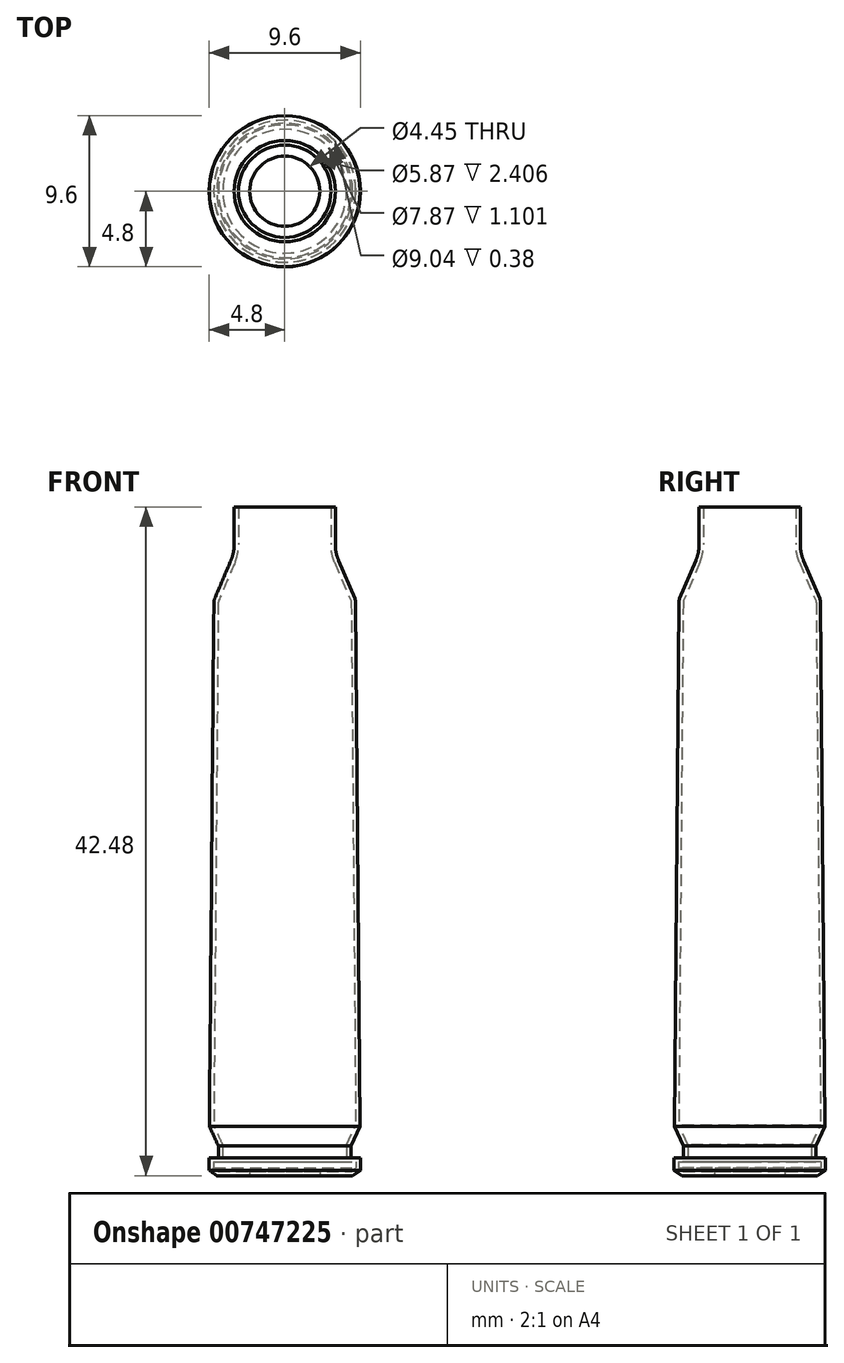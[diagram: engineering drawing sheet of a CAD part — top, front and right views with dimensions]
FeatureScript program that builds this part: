
annotation { "Feature Type Name" : "Feature", "Feature Type Description" : "" }
export const myFeature = defineFeature(function(context is Context, id is Id, definition is map)
    precondition{}
    {
        {
            var Q0;
            Q0=qCreatedBy(makeId("Front.planeOp"),FACE);
            var sketch = newSketch(context, id + "F0", { "sketchPlane" : qUnion([Q0])});
            skLineSegment(sketch, "E0", {"start": v(4.31, -41.16) * mm, "end": v(4.8, -40.82) * mm});
            skLineSegment(sketch, "E1", {"start": v(4.8, -40.82) * mm, "end": v(4.8, -40.01) * mm});
            skLineSegment(sketch, "E2", {"start": v(4.8, -40.01) * mm, "end": v(4.22, -40.01) * mm});
            skLineSegment(sketch, "E3", {"start": v(4.22, -40.01) * mm, "end": v(4.22, -39.25) * mm});
            skLineSegment(sketch, "E4", {"start": v(4.22, -39.25) * mm, "end": v(4.79, -38.02) * mm});
            skLineSegment(sketch, "E5", {"start": v(4.79, -38.02) * mm, "end": v(4.5, -4.76) * mm});
            skPoint(sketch, "E6", {"position": v(0, 5.97) * mm});
            skLineSegment(sketch, "E7", {"start": v(4.45, -4.52) * mm, "end": v(3.42, -2.08) * mm});
            skLineSegment(sketch, "E8", {"start": v(3.22, 1.32) * mm, "end": v(3.22, -1.09) * mm});
            skPoint(sketch, "E9.visualSharp", {"position": v(4.5, -4.63) * mm});
            skArc(sketch, "E9.filletArc", {"start": v(4.5, -4.76) * mm, "mid": v(4.49, -4.64) * mm, "end": v(4.45, -4.52) * mm});
            skPoint(sketch, "E10.visualSharp", {"position": v(3.22, -1.6) * mm});
            skArc(sketch, "E10.filletArc", {"start": v(3.22, -1.09) * mm, "mid": v(3.27, -1.6) * mm, "end": v(3.42, -2.08) * mm});
            skLineSegment(sketch, "E11", {"start": v(0, -41.15) * mm, "end": v(0, 1.32) * mm});
            skLineSegment(sketch, "E12", {"start": v(4.31, -41.16) * mm, "end": v(2.23, -41.16) * mm});
            skLineSegment(sketch, "E13.2", {"start": v(4.52, -40.3) * mm, "end": v(3.94, -40.3) * mm});
            skLineSegment(sketch, "E13.3", {"start": v(4.52, -40.67) * mm, "end": v(4.52, -40.3) * mm});
            skLineSegment(sketch, "E13.4", {"start": v(4.23, -40.88) * mm, "end": v(4.52, -40.67) * mm});
            skLineSegment(sketch, "E13.5", {"start": v(4.23, -40.88) * mm, "end": v(2.23, -40.88) * mm});
            skLineSegment(sketch, "E13.6", {"start": v(3.94, -40.3) * mm, "end": v(3.94, -39.2) * mm});
            skLineSegment(sketch, "E13.7", {"start": v(3.94, -39.2) * mm, "end": v(4.5, -37.96) * mm});
            skLineSegment(sketch, "E13.8", {"start": v(4.5, -37.96) * mm, "end": v(4.22, -4.76) * mm});
            skArc(sketch, "E13.9", {"start": v(4.22, -4.76) * mm, "mid": v(4.22, -4.7) * mm, "end": v(4.2, -4.63) * mm});
            skLineSegment(sketch, "E13.10", {"start": v(4.2, -4.63) * mm, "end": v(3.16, -2.19) * mm});
            skArc(sketch, "E13.11", {"start": v(2.94, -1.09) * mm, "mid": v(3, -1.65) * mm, "end": v(3.16, -2.19) * mm});
            skLineSegment(sketch, "E14", {"start": v(2.23, -41.16) * mm, "end": v(2.23, -40.88) * mm});
            skLineSegment(sketch, "E15", {"start": v(2.94, -1.09) * mm, "end": v(2.94, 1.32) * mm});
            skLineSegment(sketch, "E16", {"start": v(2.94, 1.32) * mm, "end": v(3.22, 1.32) * mm});
            skSolve(sketch);
        }
        {
            var Q0;
            Q0=qSketchRegion(id+"F0",true);
            var Q1;
            Q1=sQuery(id+"F0.wireOp",EDGE,"E11");
            revolve(context, id + "F1", {"entities" : qUnion([Q0]), "axis" : qUnion([Q1]), "revolveType" : RevolveType.FULL});
        }
    });
